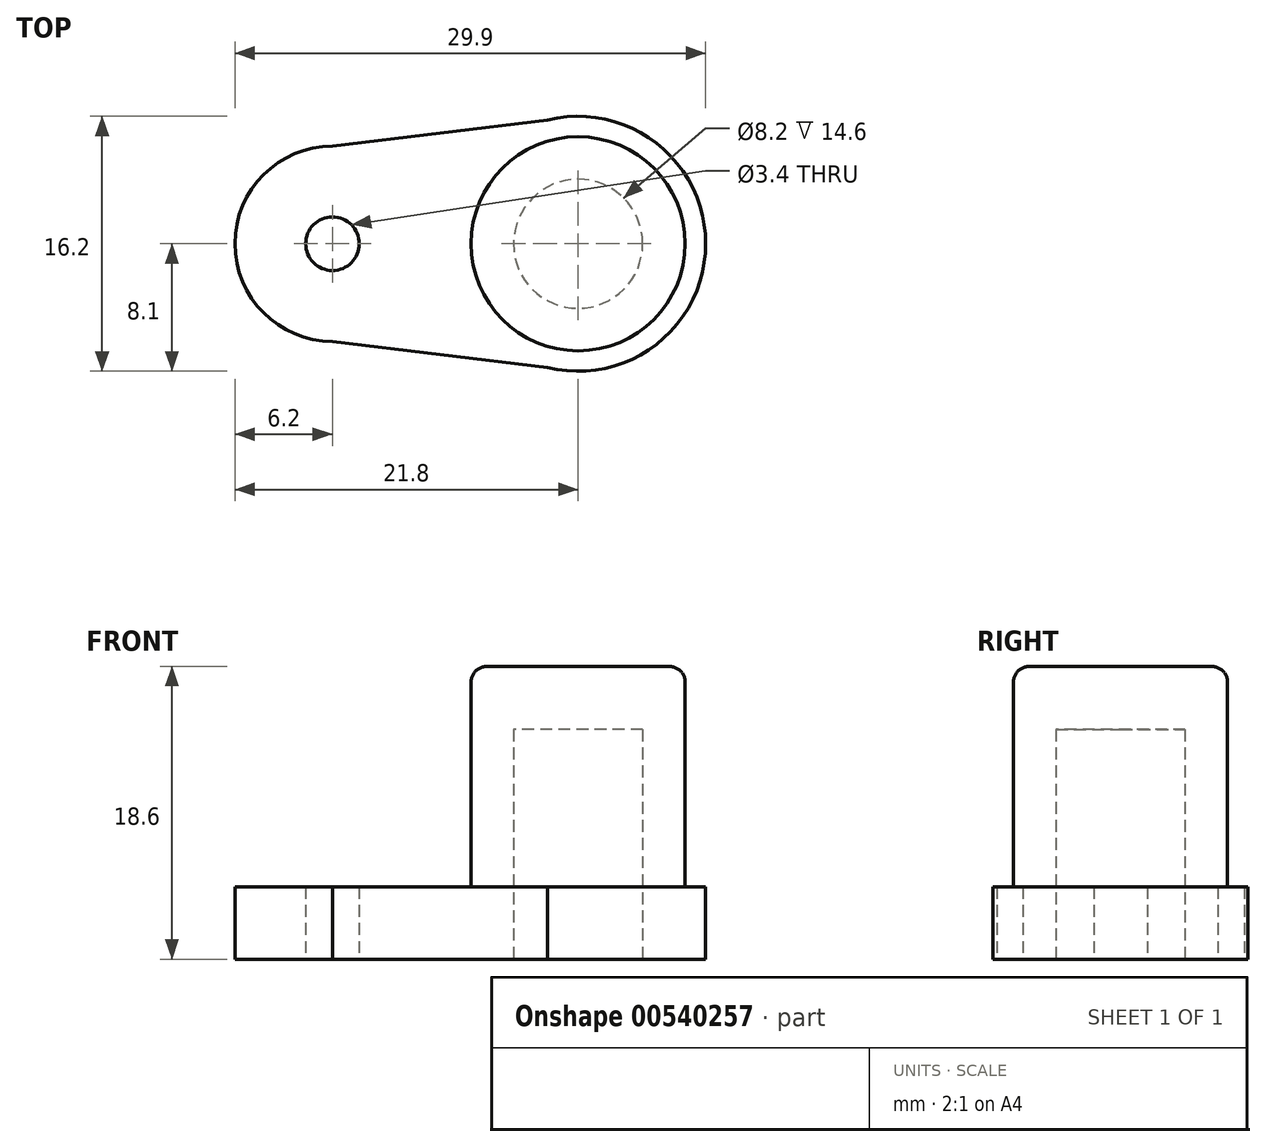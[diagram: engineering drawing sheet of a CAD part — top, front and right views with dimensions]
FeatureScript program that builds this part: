
annotation { "Feature Type Name" : "Feature", "Feature Type Description" : "" }
export const myFeature = defineFeature(function(context is Context, id is Id, definition is map)
    precondition{}
    {
        {
            var Q0;
            Q0=qCreatedBy(makeId("Top.planeOp"),FACE);
            var sketch = newSketch(context, id + "F0", { "sketchPlane" : qUnion([Q0])});
            skCircle(sketch, "E0", {"center": v(0, 0) * mm, "radius": 4.1 * mm});
            skCircle(sketch, "E1", {"center": v(-15.6, 0) * mm, "radius": 1.7 * mm});
            skCircle(sketch, "E2", {"center": v(-15.6, 0) * mm, "radius": 6.2 * mm});
            skCircle(sketch, "E3", {"center": v(0, 0) * mm, "radius": 8.1 * mm});
            skLineSegment(sketch, "E4", {"start": v(-15.6, 6.2) * mm, "end": v(0, 8.1) * mm});
            skLineSegment(sketch, "E5.MirrorCS", {"start": v(-15.6, -6.2) * mm, "end": v(0, -8.1) * mm});
            skSolve(sketch);
        }
        {
            var Q0;
            Q0 = qSketchRegion(id + "F0", true);
            extrude(context, id + "F1", {"entities" : qUnion([Q0]), "depth" : 4.6 * mm, "offsetDistance" : 25 * mm});
        }
        {
            var Q0;
            Q0=makeQuery(id+"F1.opExtrude","CAP_FACE",FACE,{"disambiguationData":[OSD([sQuery(id+"F0.wireOp",EDGE,"E0"),sQuery(id+"F0.wireOp",EDGE,"E1"),sQuery(id+"F0.wireOp",EDGE,"E2"),sQuery(id+"F0.wireOp",EDGE,"E3"),sQuery(id+"F0.wireOp",EDGE,"E4"),sQuery(id+"F0.wireOp",EDGE,"E5.MirrorCS")])],"isStart":false});
            var sketch = newSketch(context, id + "F2", { "sketchPlane" : qUnion([Q0])});
            skCircle(sketch, "E6", {"center": v(0, 0) * mm, "radius": 6.8 * mm});
            skSolve(sketch);
        }
        {
            var Q0;
            Q0 = qSketchRegion(id + "F2", true);
            extrude(context, id + "F3", {"entities" : qUnion([Q0]), "operationType" : NewBodyOperationType.ADD, "depth" : 14 * mm, "offsetDistance" : 25 * mm});
        }
        {
            var Q0;
            Q0=makeQuery(id+"F3.opExtrude","CAP_FACE",FACE,{"disambiguationData":[OSD([sQuery(id+"F2.wireOp",EDGE,"E6")])],"isStart":true});
            extrude(context, id + "F4", {"entities" : qUnion([Q0]), "operationType" : NewBodyOperationType.REMOVE, "oppositeDirection" : true, "depth" : 10 * mm, "offsetDistance" : 25 * mm});
        }
        {
            var Q0;
            Q0=makeQuery(id+"F3.opExtrude","CAP_EDGE",EDGE,{"disambiguationData":[OSD([sQuery(id+"F2.wireOp",EDGE,"E6")])],"isStart":true});
            var Q1;
            Q1=makeQuery(id+"F3.opExtrude","CAP_EDGE",EDGE,{"disambiguationData":[OSD([sQuery(id+"F2.wireOp",EDGE,"E6")])],"isStart":false});
            fillet(context, id + "F5", {"entities" : qUnion([Q0, Q1]), "radius" : 1 * mm, "tangentPropagation" : true, "allowEdgeOverflow" : false});
        }
    });
